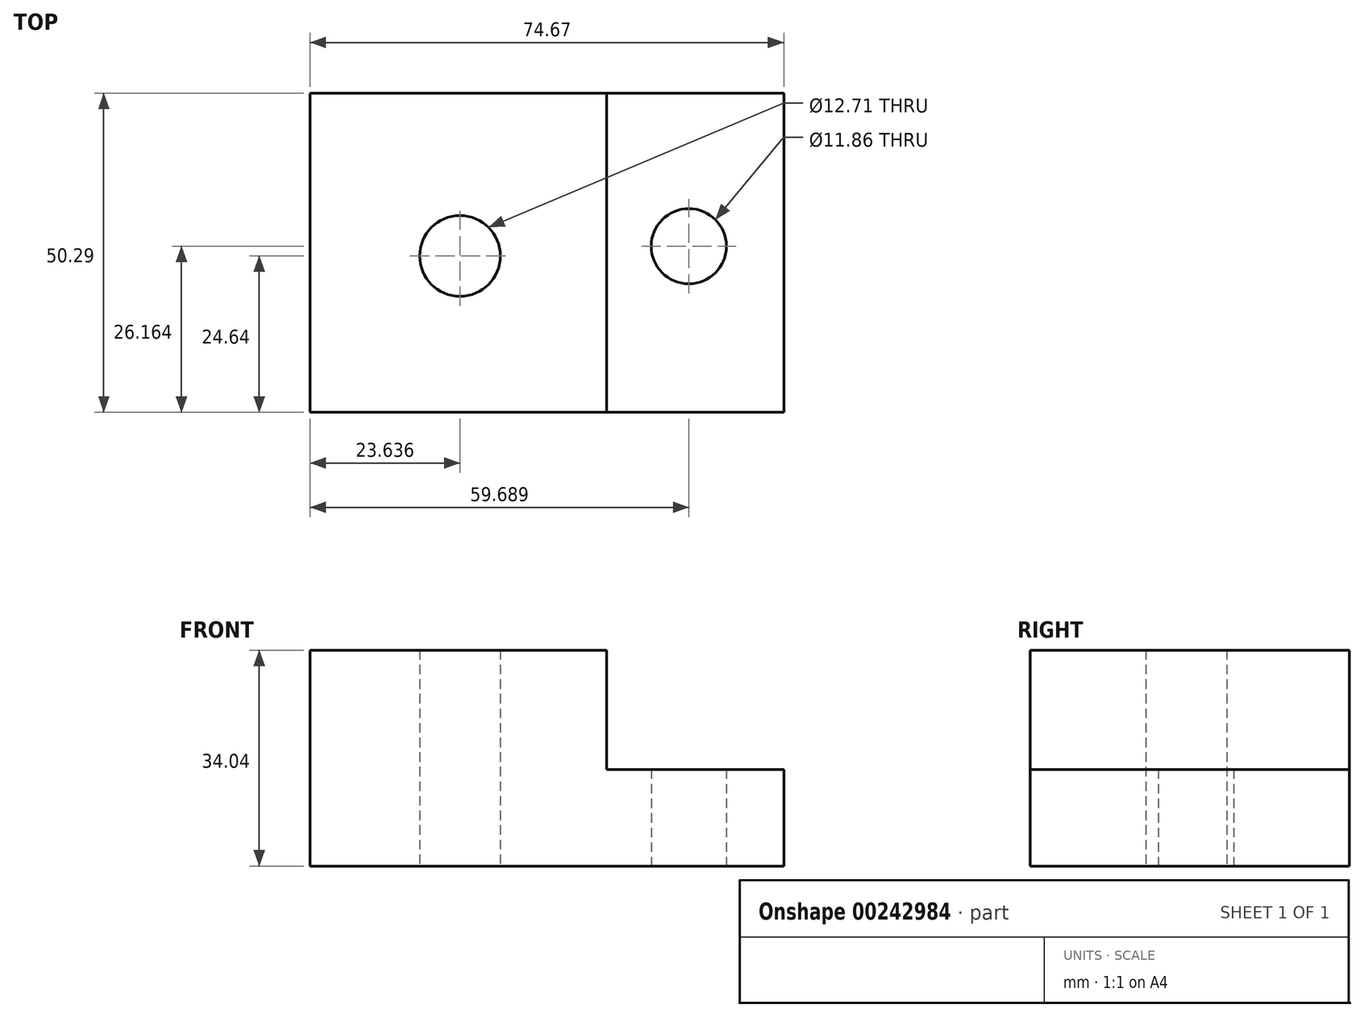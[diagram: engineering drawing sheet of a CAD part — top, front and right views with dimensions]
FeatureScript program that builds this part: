
annotation { "Feature Type Name" : "Feature", "Feature Type Description" : "" }
export const myFeature = defineFeature(function(context is Context, id is Id, definition is map)
    precondition{}
    {
        {
            var Q0;
            Q0=qCreatedBy(makeId("Top.planeOp"),FACE);
            var sketch = newSketch(context, id + "F0", { "sketchPlane" : qUnion([Q0])});
            skLineSegment(sketch, "E0.bottom", {"start": v(-31.85, 32) * mm, "end": v(14.88, 32) * mm});
            skLineSegment(sketch, "E0.top", {"start": v(-31.85, -18.29) * mm, "end": v(14.88, -18.29) * mm});
            skLineSegment(sketch, "E0.left", {"start": v(-31.85, 32) * mm, "end": v(-31.85, -18.29) * mm});
            skLineSegment(sketch, "E0.right", {"start": v(14.88, 32) * mm, "end": v(14.88, -18.29) * mm});
            skLineSegment(sketch, "E1", {"start": v(-31.85, 6.86) * mm, "end": v(-14.07, 6.86) * mm, "construction": true});
            skLineSegment(sketch, "E2", {"start": v(14.88, 6.86) * mm, "end": v(-1.88, 6.86) * mm, "construction": true});
            skPoint(sketch, "E2.endSnap0", {"position": v(14.88, 6.86) * mm});
            skLineSegment(sketch, "E3", {"start": v(-8.48, 32) * mm, "end": v(-8.48, 12.7) * mm, "construction": true});
            skLineSegment(sketch, "E4", {"start": v(-8.48, -18.29) * mm, "end": v(-8.48, 0) * mm, "construction": true});
            skCircle(sketch, "E5", {"center": v(-8.21, 6.35) * mm, "radius": 6.36 * mm});
            skLineSegment(sketch, "E6.bottom", {"start": v(14.88, 32) * mm, "end": v(42.82, 32) * mm});
            skLineSegment(sketch, "E6.top", {"start": v(14.88, -18.29) * mm, "end": v(42.82, -18.29) * mm});
            skLineSegment(sketch, "E6.right", {"start": v(42.82, 32) * mm, "end": v(42.82, -18.29) * mm});
            skLineSegment(sketch, "E7", {"start": v(42.82, 6.86) * mm, "end": v(33.68, 6.86) * mm});
            skLineSegment(sketch, "E8", {"start": v(28.85, 32) * mm, "end": v(28.85, 13.72) * mm});
            skLineSegment(sketch, "E9", {"start": v(28.85, -18.29) * mm, "end": v(28.85, 2.03) * mm});
            skCircle(sketch, "E10", {"center": v(27.84, 7.87) * mm, "radius": 5.93 * mm});
            skSolve(sketch);
        }
        {
            var Q0;
            Q0=makeQuery(id+"F0.imprint","IMPRINT",FACE,{"disambiguationData":[TD([[makeQuery(id+"F0.imprint","IMPRINT",EDGE,{"derivedFrom":sQuery(id+"F0.wireOp",EDGE,"E0.bottom")}),-1.0]])]});
            extrude(context, id + "F1", {"entities" : qUnion([Q0]), "depth" : 34.04 * mm});
        }
        {
            var Q0;
            {var subQ5=sQuery(id+"F0.wireOp",EDGE,"E7");Q0=makeQuery(id+"F0.imprint","IMPRINT",FACE,{"disambiguationData":[TD([[makeQuery(id+"F0.imprint","IMPRINT",EDGE,{"derivedFrom":subQ5}),-1.0]])]});}
            var Q1;
            {var subQ1=sQuery(id+"F0.wireOp",EDGE,"E0.right");Q1=makeQuery(id+"F0.imprint","IMPRINT",FACE,{"disambiguationData":[TD([[makeQuery(id+"F0.imprint","IMPRINT",EDGE,{"derivedFrom":subQ1}),1.0]])]});}
            var Q2;
            {var subQ1=sQuery(id+"F0.wireOp",EDGE,"E7");Q2=makeQuery(id+"F0.imprint","IMPRINT",FACE,{"disambiguationData":[TD([[makeQuery(id+"F0.imprint","IMPRINT",EDGE,{"derivedFrom":subQ1}),1.0]])]});}
            extrude(context, id + "F2", {"entities" : qUnion([Q0, Q1, Q2]), "operationType" : NewBodyOperationType.ADD, "depth" : 15.24 * mm});
        }
    });
